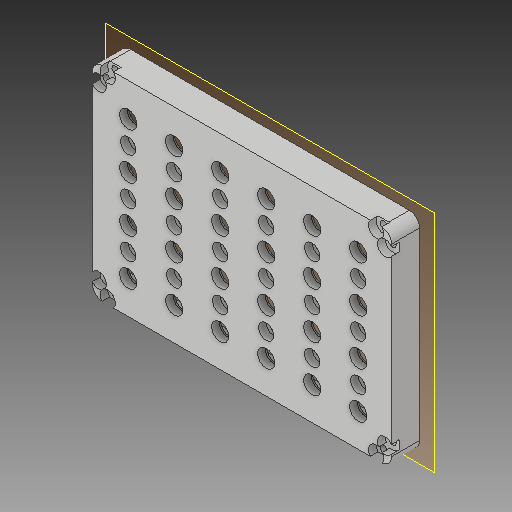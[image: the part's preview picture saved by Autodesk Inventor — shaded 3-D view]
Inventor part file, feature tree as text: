
AUTODESK INVENTOR PART (.ipt)
format: ipt  version: 2019.4 (Build 234330000, 330)  size: 534,016 bytes
history: native  units: mm
features: other x7, sketch x6, reference x6, extrude x4, projected_geometry x3, plane x2, pattern_linear x2, hole x2, shell x1
ambient origin geometry x8: Origin, YZ Plane, XZ Plane, XY Plane, X Axis, Y Axis, Z Axis, Center Point
bodies: Solid1 (feature_tree)
feature tree (33):
  plane  "Work Plane1"
  sketch  "Sketch1"  dims[d0=10.0mm d1=0.0mm d2=4.0mm d3=0.0mm]
  plane  "Work Plane2"
  extrude  "Extrusion1"  Depth=4.0mm TaperAngle=0.0deg
  extrude  "Extrusion2"  Depth=4.0mm TaperAngle=0.0deg
  extrude  "Extrusion3"  Depth=1.0mm
  extrude  "Extrusion4"  Depth=1.0mm
  pattern_linear  "Rectangular Pattern1"  Count1=6 Spacing1=18.0mm
  hole  "Hole1"  [1 undecoded]
  hole  "Hole2"  [1 undecoded]
  pattern_linear  "Rectangular Pattern2"  [2 undecoded]
  shell  "Shell1"  [1 undecoded]
  reference  "Reference1"
  sketch  "Sketch2"  dims[d4=6.75mm d5=4.0mm d6=0.0mm]
  projected_geometry  "Projected Loop1"
  sketch  "Sketch3"  dims[d7=1.0mm d8=0.0mm d9=60.0mm d11=18.0mm]
  reference  "Reference2"
  reference  "Reference3"
  sketch  "Sketch4"  dims[d12=40.0mm d14=18.0mm]
  reference  "Reference4"
  sketch  "Sketch5"  dims[d15=2.8mm d16=6.0mm d17=6.0mm d18=3.0mm d19=90.0deg d20=12.0mm d21=20.594885mm]
  projected_geometry  "Projected Loop2"
  sketch  "Sketch6"  dims[d22=3.0mm d23=6.0mm d24=6.0mm d25=3.0mm d26=90.0deg d27=12.0mm d28=20.594885mm d29=30.0mm d31=18.0mm d32=60.0mm d34=18.0mm d35=1.0mm]
  projected_geometry  "Projected Loop3"
  reference  "Reference5"
  reference  "Reference6"
  other  "Full_HITscope_v0.iam"
  other  "05_Omniscope_base_v1:1"
  other  "00_OV_lens:3"
  other  "Assembly_Omniscope_v1:11"
  other  "01_Camera_Module_left_v0:1"
  other  "00_OV_lens:1"
  other  "Assembly_Omniscope_v1:12"
note: 5 required parameter values undecoded (feature->parameter linkage not recoverable at this tier; creation-order binding heuristic only, values carry confidence <= 0.55)
